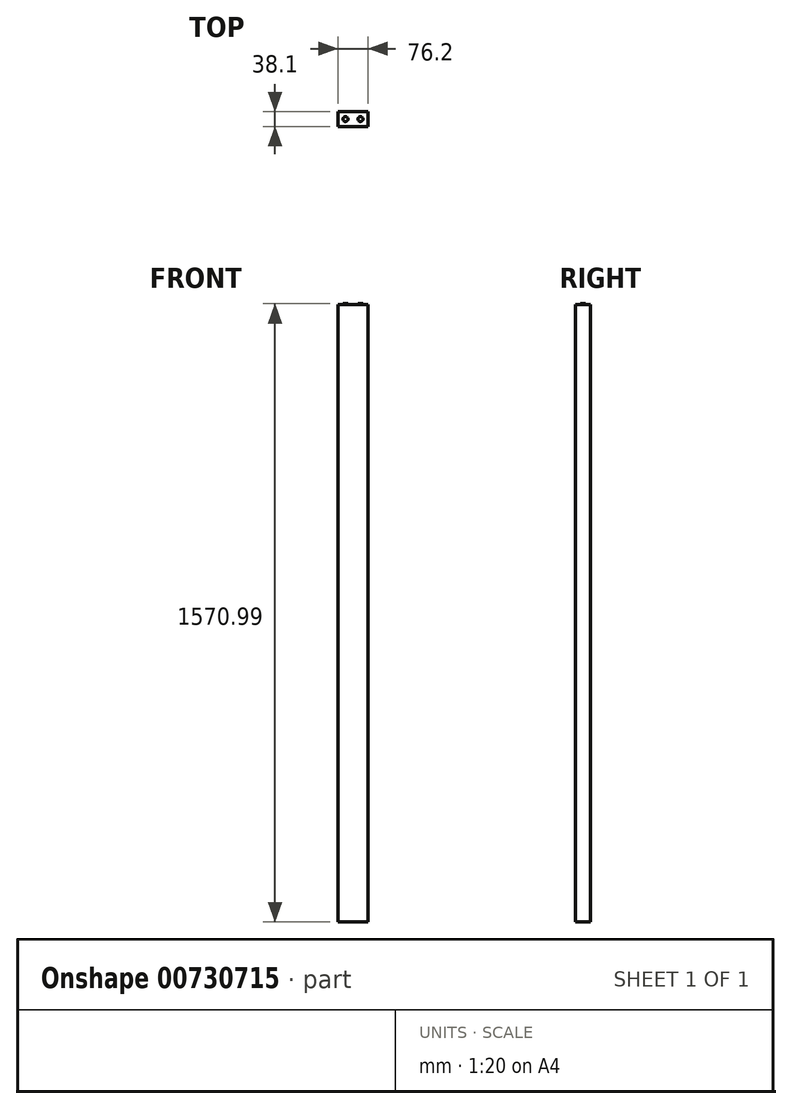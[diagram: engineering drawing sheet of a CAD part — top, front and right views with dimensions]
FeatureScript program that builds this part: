
annotation { "Feature Type Name" : "Feature", "Feature Type Description" : "" }
export const myFeature = defineFeature(function(context is Context, id is Id, definition is map)
    precondition{}
    {
        {
            var Q0;
            Q0=qCreatedBy(makeId("Top.planeOp"),FACE);
            var sketch = newSketch(context, id + "F0", { "sketchPlane" : qUnion([Q0])});
            skLineSegment(sketch, "E0.bottom", {"start": v(38.1, -19.05) * mm, "end": v(-38.1, -19.05) * mm});
            skLineSegment(sketch, "E0.top", {"start": v(38.1, 19.05) * mm, "end": v(-38.1, 19.05) * mm});
            skLineSegment(sketch, "E0.left", {"start": v(38.1, -19.05) * mm, "end": v(38.1, 19.05) * mm});
            skLineSegment(sketch, "E0.right", {"start": v(-38.1, -19.05) * mm, "end": v(-38.1, 19.05) * mm});
            skPoint(sketch, "E0.middle", {"position": v(0, 0) * mm});
            skSolve(sketch);
        }
        {
            var Q0;
            Q0=makeQuery(id+"F0.imprint","IMPRINT",FACE,{"disambiguationData":[TD([[makeQuery(id+"F0.imprint","IMPRINT",EDGE,{"derivedFrom":sQuery(id+"F0.wireOp",EDGE,"E0.bottom")}),-1.0]])]});
            extrude(context, id + "F1", {"entities" : qUnion([Q0]), "depth" : 1568.45 * mm, "offsetDistance" : 25.4 * mm});
        }
        {
            var Q0;
            Q0=makeQuery(id+"F1.opExtrude","CAP_FACE",FACE,{"disambiguationData":[OSD([sQuery(id+"F0.wireOp",EDGE,"E0.bottom"),sQuery(id+"F0.wireOp",EDGE,"E0.top"),sQuery(id+"F0.wireOp",EDGE,"E0.left"),sQuery(id+"F0.wireOp",EDGE,"E0.right")])],"isStart":false});
            var sketch = newSketch(context, id + "F2", { "sketchPlane" : qUnion([Q0])});
            skLineSegment(sketch, "E1.bottom", {"start": v(0, 19.05) * mm, "end": v(-38.1, 19.05) * mm});
            skLineSegment(sketch, "E1.top", {"start": v(0, -19.05) * mm, "end": v(-38.1, -19.05) * mm});
            skLineSegment(sketch, "E1.left", {"start": v(0, 19.05) * mm, "end": v(0, -19.05) * mm});
            skLineSegment(sketch, "E1.right", {"start": v(-38.1, 19.05) * mm, "end": v(-38.1, -19.05) * mm});
            skLineSegment(sketch, "E2.bottom", {"start": v(0, 19.05) * mm, "end": v(38.1, 19.05) * mm});
            skLineSegment(sketch, "E2.top", {"start": v(0, -19.05) * mm, "end": v(38.1, -19.05) * mm});
            skLineSegment(sketch, "E2.right", {"start": v(38.1, 19.05) * mm, "end": v(38.1, -19.05) * mm});
            skCircle(sketch, "E3", {"center": v(-19.05, 0) * mm, "radius": 6.35 * mm});
            skPoint(sketch, "E3.centerSnap0", {"position": v(-19.05, 19.05) * mm});
            skCircle(sketch, "E4", {"center": v(19.05, 0) * mm, "radius": 6.35 * mm});
            skPoint(sketch, "E4.centerSnap0", {"position": v(19.05, 19.05) * mm});
            skSolve(sketch);
        }
        {
            var Q0;
            Q0=makeQuery(id+"F2.imprint","IMPRINT",FACE,{"disambiguationData":[TD([[makeQuery(id+"F2.imprint","IMPRINT",EDGE,{"derivedFrom":sQuery(id+"F2.wireOp",EDGE,"E3")}),1.0]])]});
            var Q1;
            Q1=makeQuery(id+"F2.imprint","IMPRINT",FACE,{"disambiguationData":[TD([[makeQuery(id+"F2.imprint","IMPRINT",EDGE,{"derivedFrom":sQuery(id+"F2.wireOp",EDGE,"E4")}),1.0]])]});
            extrude(context, id + "F3", {"entities" : qUnion([Q0, Q1]), "operationType" : NewBodyOperationType.ADD, "depth" : 2.54 * mm, "offsetDistance" : 25.4 * mm});
        }
    });
